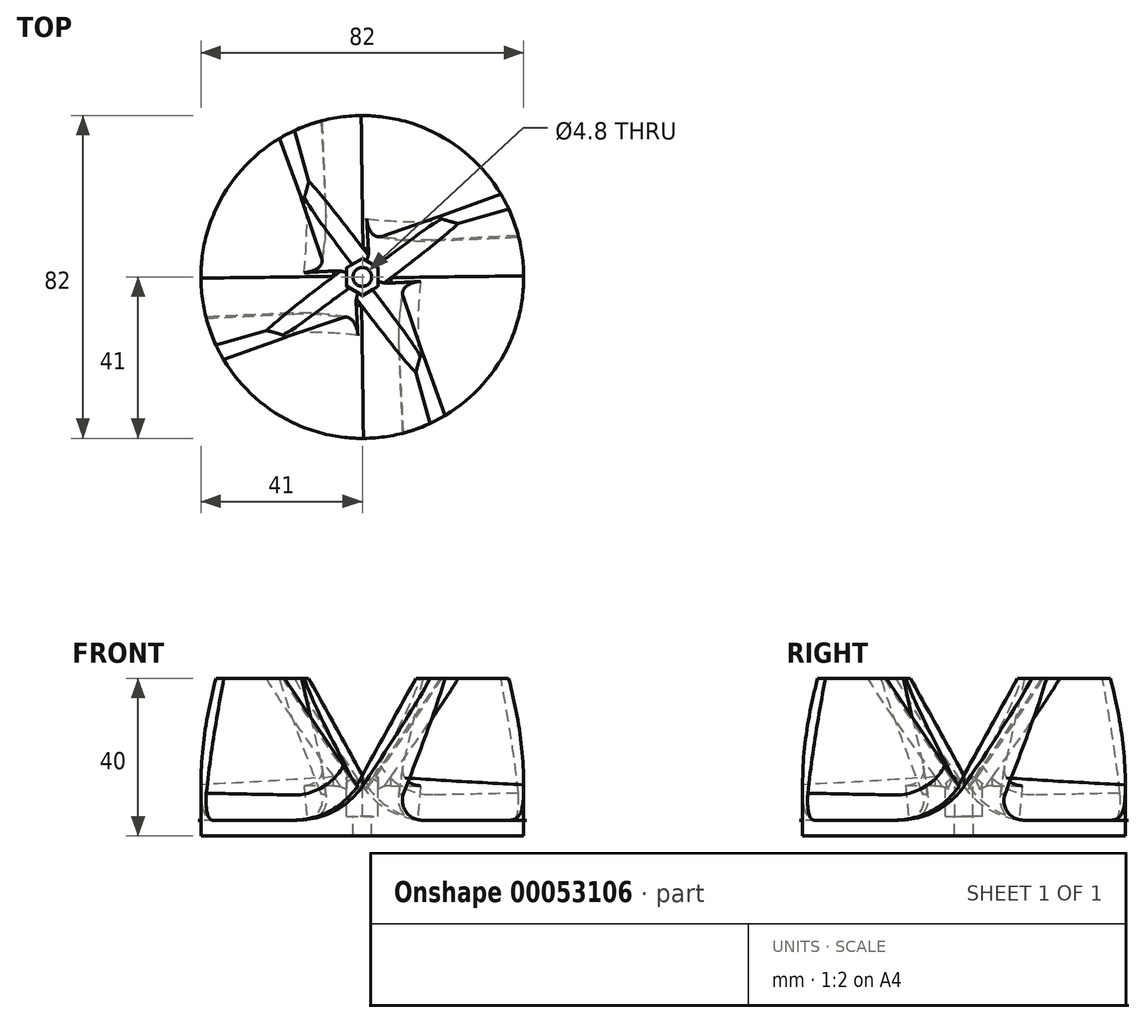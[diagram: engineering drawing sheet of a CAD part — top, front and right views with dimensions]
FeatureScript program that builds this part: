
annotation { "Feature Type Name" : "Feature", "Feature Type Description" : "" }
export const myFeature = defineFeature(function(context is Context, id is Id, definition is map)
    precondition{}
    {
        {
            var Q0;
            Q0=qCreatedBy(makeId("Top.planeOp"),FACE);
            var sketch = newSketch(context, id + "F0", { "sketchPlane" : qUnion([Q0])});
            skLineSegment(sketch, "E0.bottom", {"start": v(7.1, 8.27) * mm, "end": v(-43.93, 8.27) * mm});
            skLineSegment(sketch, "E0.top", {"start": v(7.1, -6.26) * mm, "end": v(-43.93, -6.26) * mm});
            skLineSegment(sketch, "E0.left", {"start": v(7.1, 8.27) * mm, "end": v(7.1, -6.26) * mm});
            skLineSegment(sketch, "E0.right", {"start": v(-43.93, 8.27) * mm, "end": v(-43.93, -6.26) * mm});
            skSolve(sketch);
        }
        {
            var Q0;
            Q0=qCreatedBy(makeId("Top.planeOp"),FACE);
            var sketch = newSketch(context, id + "F1", { "sketchPlane" : qUnion([Q0])});
            skCircle(sketch, "E1", {"center": v(0, 0) * mm, "radius": 41 * mm});
            skCircle(sketch, "E2", {"center": v(0, 0) * mm, "radius": 83.6 * mm});
            skSolve(sketch);
        }
        {
            var Q0;
            Q0=makeQuery(id+"F1.imprint","IMPRINT",FACE,{"disambiguationData":[TD([[makeQuery(id+"F1.imprint","IMPRINT",EDGE,{"derivedFrom":sQuery(id+"F1.wireOp",EDGE,"E1")}),1.0]])]});
            extrude(context, id + "F2", {"entities" : qUnion([Q0]), "depth" : 4 * mm});
        }
        {
            var Q0;
            Q0=qCreatedBy(makeId("Top.planeOp"),FACE);
            cPlane(context, id + "F3", {"entities" : qUnion([Q0]), "cplaneType" : CPlaneType.OFFSET, "offset" : 40 * mm, "width" : 150 * mm, "height" : 150 * mm});
        }
        {
            var Q0;
            Q0=qCreatedBy(id+"F3.planeOp",FACE);
            var sketch = newSketch(context, id + "F4", { "sketchPlane" : qUnion([Q0])});
            skCircle(sketch, "E3", {"center": v(0, 0) * mm, "radius": 25 * mm});
            skCircle(sketch, "E4", {"center": v(0, 0) * mm, "radius": 45 * mm});
            skLineSegment(sketch, "E5", {"start": v(-39.03, -22.4) * mm, "end": v(-19.7, -15.4) * mm});
            skLineSegment(sketch, "E6", {"start": v(-21.49, -12.78) * mm, "end": v(-41.08, -18.37) * mm});
            skCircle(sketch, "E7", {"center": v(0, 0) * mm, "radius": 2.4 * mm});
            skCircle(sketch, "E8.cCircle", {"center": v(0, 0) * mm, "radius": 4.05 * mm, "construction": true});
            skLineSegment(sketch, "E8.0", {"start": v(4.05, 2.34) * mm, "end": v(4.05, -2.34) * mm});
            skLineSegment(sketch, "E8.1", {"start": v(4.05, -2.34) * mm, "end": v(0, -4.68) * mm});
            skLineSegment(sketch, "E8.2", {"start": v(0, -4.68) * mm, "end": v(-4.05, -2.34) * mm});
            skLineSegment(sketch, "E8.3", {"start": v(-4.05, -2.34) * mm, "end": v(-4.05, 2.34) * mm});
            skLineSegment(sketch, "E8.4", {"start": v(-4.05, 2.34) * mm, "end": v(0, 4.68) * mm});
            skLineSegment(sketch, "E8.5", {"start": v(0, 4.68) * mm, "end": v(4.05, 2.34) * mm});
            skPoint(sketch, "E8.0.midPoint", {"position": v(4.05, 0) * mm});
            skSolve(sketch);
        }
        {
            var Q0;
            {var subQ1=sQuery(id+"F4.wireOp",EDGE,"E5");Q0=makeQuery(id+"F4.imprint","IMPRINT",FACE,{"disambiguationData":[TD([[makeQuery(id+"F4.imprint","IMPRINT",EDGE,{"derivedFrom":subQ1}),1.0]])]});}
            var Q1;
            {var subQ0=sQuery(id+"F0.wireOp",EDGE,"E0.left");Q1=makeQuery(id+"F0.imprint","IMPRINT",FACE,{"disambiguationData":[TD([[makeQuery(id+"F0.imprint","IMPRINT",EDGE,{"derivedFrom":subQ0}),-1.0]])]});}
            loft(context, id + "F5", {"sheetProfilesArray" : [{ "sheetProfileEntities" : qUnion([Q0]) }, { "sheetProfileEntities" : qUnion([Q1]) }]});
        }
        {
            var Q0;
            Q0=makeQuery(id+"F5.opLoft","SWEPT_EDGE",EDGE,{"disambiguationData":[OSD([sQuery(id+"F0.wireOp",EDGE,"E0.bottom"),sQuery(id+"F0.wireOp",EDGE,"E0.left"),sQuery(id+"F4.wireOp",EDGE,"E3"),sQuery(id+"F4.wireOp",EDGE,"E6")])]});
            chamfer(context, id + "F6", {"entities" : qUnion([Q0]), "width" : 3 * mm, "tangentPropagation" : true});
        }
        {
            var Q0;
            {var subQ1=sQuery(id+"F0.wireOp",EDGE,"2f4ce80c-512e-42e9-ad37-1b76bf56904e");var subQ4=sQuery(id+"F4.wireOp",EDGE,"E5");Q0=makeQuery(id+"F5.opLoft","SWEPT_BODY",BODY,{"disambiguationData":[OSD([makeQuery(id+"F0.imprint","IMPRINT",FACE,{"disambiguationData":[TD([[makeQuery(id+"F0.imprint","IMPRINT",EDGE,{"derivedFrom":subQ1}),-1.0]])]}),makeQuery(id+"F4.imprint","IMPRINT",FACE,{"disambiguationData":[TD([[makeQuery(id+"F4.imprint","IMPRINT",EDGE,{"derivedFrom":subQ4}),1.0]])]})])]});}
            var Q1;
            Q1=makeQuery(id+"F2.opExtrude","CAP_EDGE",EDGE,{"disambiguationData":[OSD([sQuery(id+"F1.wireOp",EDGE,"E1")])],"isStart":false});
            circularPattern(context, id + "F7", {"entities" : qUnion([Q0]), "axis" : qUnion([Q1]), "angle" : 90 * degree, "instanceCount" : round(4), "computeTransformsWithoutBuiltin" : true});
        }
        {
            var Q0;
            {var subQ4=sQuery(id+"F0.wireOp",EDGE,"5ef0fec1-321e-4ed4-9ece-5ae84b4b1e6a.bottom");var subQ6=sQuery(id+"F4.wireOp",EDGE,"E5");Q0=makeQuery(id+"F5.opLoft","SWEPT_BODY",BODY,{"disambiguationData":[OSD([makeQuery(id+"F0.imprint","IMPRINT",FACE,{"disambiguationData":[TD([[makeQuery(id+"F0.imprint","IMPRINT",EDGE,{"derivedFrom":subQ4}),-1.0]])]}),makeQuery(id+"F4.imprint","IMPRINT",FACE,{"disambiguationData":[TD([[makeQuery(id+"F4.imprint","IMPRINT",EDGE,{"derivedFrom":subQ6}),1.0]])]})])]});}
            var Q1;
            {var subQ4=sQuery(id+"F0.wireOp",EDGE,"5ef0fec1-321e-4ed4-9ece-5ae84b4b1e6a.bottom");var subQ6=sQuery(id+"F4.wireOp",EDGE,"E5");Q1=makeQuery(id+"F7.opPattern","COPY",BODY,{"derivedFrom":makeQuery(id+"F5.opLoft","SWEPT_BODY",BODY,{"disambiguationData":[OSD([makeQuery(id+"F0.imprint","IMPRINT",FACE,{"disambiguationData":[TD([[makeQuery(id+"F0.imprint","IMPRINT",EDGE,{"derivedFrom":subQ4}),-1.0]])]}),makeQuery(id+"F4.imprint","IMPRINT",FACE,{"disambiguationData":[TD([[makeQuery(id+"F4.imprint","IMPRINT",EDGE,{"derivedFrom":subQ6}),1.0]])]})])]}),"instanceName":"2"});}
            var Q2;
            {var subQ4=sQuery(id+"F0.wireOp",EDGE,"5ef0fec1-321e-4ed4-9ece-5ae84b4b1e6a.bottom");var subQ6=sQuery(id+"F4.wireOp",EDGE,"E5");Q2=makeQuery(id+"F7.opPattern","COPY",BODY,{"derivedFrom":makeQuery(id+"F5.opLoft","SWEPT_BODY",BODY,{"disambiguationData":[OSD([makeQuery(id+"F0.imprint","IMPRINT",FACE,{"disambiguationData":[TD([[makeQuery(id+"F0.imprint","IMPRINT",EDGE,{"derivedFrom":subQ4}),-1.0]])]}),makeQuery(id+"F4.imprint","IMPRINT",FACE,{"disambiguationData":[TD([[makeQuery(id+"F4.imprint","IMPRINT",EDGE,{"derivedFrom":subQ6}),1.0]])]})])]}),"instanceName":"1"});}
            var Q3;
            {var subQ4=sQuery(id+"F0.wireOp",EDGE,"5ef0fec1-321e-4ed4-9ece-5ae84b4b1e6a.bottom");var subQ6=sQuery(id+"F4.wireOp",EDGE,"E5");Q3=makeQuery(id+"F7.opPattern","COPY",BODY,{"derivedFrom":makeQuery(id+"F5.opLoft","SWEPT_BODY",BODY,{"disambiguationData":[OSD([makeQuery(id+"F0.imprint","IMPRINT",FACE,{"disambiguationData":[TD([[makeQuery(id+"F0.imprint","IMPRINT",EDGE,{"derivedFrom":subQ4}),-1.0]])]}),makeQuery(id+"F4.imprint","IMPRINT",FACE,{"disambiguationData":[TD([[makeQuery(id+"F4.imprint","IMPRINT",EDGE,{"derivedFrom":subQ6}),1.0]])]})])]}),"instanceName":"3"});}
            var Q4;
            Q4=makeQuery(id+"F2.opExtrude","SWEPT_BODY",BODY,{"disambiguationData":[OSD([sQuery(id+"F1.wireOp",EDGE,"E1")])]});
            booleanBodies(context, id + "F8", {"operationType" : BooleanOperationType.UNION, "tools" : qUnion([Q0, Q1, Q2, Q3, Q4])});
        }
        {
            var Q0;
            Q0=makeQuery(id+"F8.opBoolean","INTERSECT",EDGE,{"derivedFrom":[makeQuery(id+"F2.opExtrude","CAP_FACE",FACE,{"disambiguationData":[OSD([sQuery(id+"F1.wireOp",EDGE,"E1")])],"isStart":false}),makeQuery(id+"F5.opLoft","SWEPT_FACE",FACE,{"disambiguationData":[OSD([sQuery(id+"F0.wireOp",EDGE,"E0.bottom"),sQuery(id+"F0.wireOp",EDGE,"E0.left"),sQuery(id+"F0.wireOp",EDGE,"E0.right"),sQuery(id+"F4.wireOp",EDGE,"E3"),sQuery(id+"F4.wireOp",EDGE,"E4"),sQuery(id+"F4.wireOp",EDGE,"E6")])]})]});
            var Q1;
            Q1=makeQuery(id+"F8.opBoolean","INTERSECT",EDGE,{"derivedFrom":[makeQuery(id+"F2.opExtrude","CAP_FACE",FACE,{"disambiguationData":[OSD([sQuery(id+"F1.wireOp",EDGE,"E1")])],"isStart":false}),makeQuery(id+"F7.opPattern","COPY",FACE,{"derivedFrom":makeQuery(id+"F5.opLoft","SWEPT_FACE",FACE,{"disambiguationData":[OSD([sQuery(id+"F0.wireOp",EDGE,"E0.bottom"),sQuery(id+"F0.wireOp",EDGE,"E0.left"),sQuery(id+"F0.wireOp",EDGE,"E0.right"),sQuery(id+"F4.wireOp",EDGE,"E3"),sQuery(id+"F4.wireOp",EDGE,"E4"),sQuery(id+"F4.wireOp",EDGE,"E6")])]}),"instanceName":"3"})]});
            var Q2;
            Q2=makeQuery(id+"F8.opBoolean","INTERSECT",EDGE,{"derivedFrom":[makeQuery(id+"F2.opExtrude","CAP_FACE",FACE,{"disambiguationData":[OSD([sQuery(id+"F1.wireOp",EDGE,"E1")])],"isStart":false}),makeQuery(id+"F7.opPattern","COPY",FACE,{"derivedFrom":makeQuery(id+"F5.opLoft","SWEPT_FACE",FACE,{"disambiguationData":[OSD([sQuery(id+"F0.wireOp",EDGE,"E0.bottom"),sQuery(id+"F0.wireOp",EDGE,"E0.left"),sQuery(id+"F0.wireOp",EDGE,"E0.right"),sQuery(id+"F4.wireOp",EDGE,"E3"),sQuery(id+"F4.wireOp",EDGE,"E4"),sQuery(id+"F4.wireOp",EDGE,"E6")])]}),"instanceName":"1"})]});
            var Q3;
            Q3=makeQuery(id+"F8.opBoolean","INTERSECT",EDGE,{"derivedFrom":[makeQuery(id+"F2.opExtrude","CAP_FACE",FACE,{"disambiguationData":[OSD([sQuery(id+"F1.wireOp",EDGE,"E1")])],"isStart":false}),makeQuery(id+"F7.opPattern","COPY",FACE,{"derivedFrom":makeQuery(id+"F5.opLoft","SWEPT_FACE",FACE,{"disambiguationData":[OSD([sQuery(id+"F0.wireOp",EDGE,"E0.bottom"),sQuery(id+"F0.wireOp",EDGE,"E0.left"),sQuery(id+"F0.wireOp",EDGE,"E0.right"),sQuery(id+"F4.wireOp",EDGE,"E3"),sQuery(id+"F4.wireOp",EDGE,"E4"),sQuery(id+"F4.wireOp",EDGE,"E6")])]}),"instanceName":"2"})]});
            fillet(context, id + "F9", {"entities" : qUnion([Q0, Q1, Q2, Q3]), "radius" : 20 * mm, "tangentPropagation" : true, "allowEdgeOverflow" : false});
        }
        {
            var Q0;
            Q0=makeQuery(id+"F8.opBoolean","INTERSECT",EDGE,{"derivedFrom":[makeQuery(id+"F2.opExtrude","CAP_FACE",FACE,{"disambiguationData":[OSD([sQuery(id+"F1.wireOp",EDGE,"E1")])],"isStart":false}),makeQuery(id+"F5.opLoft","SWEPT_FACE",FACE,{"disambiguationData":[OSD([sQuery(id+"F0.wireOp",EDGE,"E0.top"),sQuery(id+"F0.wireOp",EDGE,"E0.left"),sQuery(id+"F0.wireOp",EDGE,"E0.right"),sQuery(id+"F4.wireOp",EDGE,"E3"),sQuery(id+"F4.wireOp",EDGE,"E4"),sQuery(id+"F4.wireOp",EDGE,"E5")])]})]});
            var Q1;
            Q1=makeQuery(id+"F8.opBoolean","INTERSECT",EDGE,{"derivedFrom":[makeQuery(id+"F2.opExtrude","CAP_FACE",FACE,{"disambiguationData":[OSD([sQuery(id+"F1.wireOp",EDGE,"E1")])],"isStart":false}),makeQuery(id+"F7.opPattern","COPY",FACE,{"derivedFrom":makeQuery(id+"F5.opLoft","SWEPT_FACE",FACE,{"disambiguationData":[OSD([sQuery(id+"F0.wireOp",EDGE,"E0.top"),sQuery(id+"F0.wireOp",EDGE,"E0.left"),sQuery(id+"F0.wireOp",EDGE,"E0.right"),sQuery(id+"F4.wireOp",EDGE,"E3"),sQuery(id+"F4.wireOp",EDGE,"E4"),sQuery(id+"F4.wireOp",EDGE,"E5")])]}),"instanceName":"1"})]});
            var Q2;
            Q2=makeQuery(id+"F8.opBoolean","INTERSECT",EDGE,{"derivedFrom":[makeQuery(id+"F2.opExtrude","CAP_FACE",FACE,{"disambiguationData":[OSD([sQuery(id+"F1.wireOp",EDGE,"E1")])],"isStart":false}),makeQuery(id+"F7.opPattern","COPY",FACE,{"derivedFrom":makeQuery(id+"F5.opLoft","SWEPT_FACE",FACE,{"disambiguationData":[OSD([sQuery(id+"F0.wireOp",EDGE,"E0.top"),sQuery(id+"F0.wireOp",EDGE,"E0.left"),sQuery(id+"F0.wireOp",EDGE,"E0.right"),sQuery(id+"F4.wireOp",EDGE,"E3"),sQuery(id+"F4.wireOp",EDGE,"E4"),sQuery(id+"F4.wireOp",EDGE,"E5")])]}),"instanceName":"2"})]});
            var Q3;
            Q3=makeQuery(id+"F8.opBoolean","INTERSECT",EDGE,{"derivedFrom":[makeQuery(id+"F2.opExtrude","CAP_FACE",FACE,{"disambiguationData":[OSD([sQuery(id+"F1.wireOp",EDGE,"E1")])],"isStart":false}),makeQuery(id+"F7.opPattern","COPY",FACE,{"derivedFrom":makeQuery(id+"F5.opLoft","SWEPT_FACE",FACE,{"disambiguationData":[OSD([sQuery(id+"F0.wireOp",EDGE,"E0.top"),sQuery(id+"F0.wireOp",EDGE,"E0.left"),sQuery(id+"F0.wireOp",EDGE,"E0.right"),sQuery(id+"F4.wireOp",EDGE,"E3"),sQuery(id+"F4.wireOp",EDGE,"E4"),sQuery(id+"F4.wireOp",EDGE,"E5")])]}),"instanceName":"3"})]});
            fillet(context, id + "F10", {"entities" : qUnion([Q0, Q1, Q2, Q3]), "radius" : 5 * mm, "tangentPropagation" : true, "allowEdgeOverflow" : false});
        }
        {
            var Q0;
            Q0=makeQuery(id+"F4.imprint","IMPRINT",FACE,{"disambiguationData":[TD([[makeQuery(id+"F4.imprint","IMPRINT",EDGE,{"derivedFrom":sQuery(id+"F4.wireOp",EDGE,"E7")}),1.0]])]});
            var Q1;
            {var subQ4=sQuery(id+"F0.wireOp",EDGE,"5ef0fec1-321e-4ed4-9ece-5ae84b4b1e6a.bottom");var subQ6=sQuery(id+"F4.wireOp",EDGE,"E5");Q1=makeQuery(id+"F7.opPattern","COPY",BODY,{"derivedFrom":makeQuery(id+"F5.opLoft","SWEPT_BODY",BODY,{"disambiguationData":[OSD([makeQuery(id+"F0.imprint","IMPRINT",FACE,{"disambiguationData":[TD([[makeQuery(id+"F0.imprint","IMPRINT",EDGE,{"derivedFrom":subQ4}),-1.0]])]}),makeQuery(id+"F4.imprint","IMPRINT",FACE,{"disambiguationData":[TD([[makeQuery(id+"F4.imprint","IMPRINT",EDGE,{"derivedFrom":subQ6}),1.0]])]})])]}),"instanceName":"2"});}
            extrude(context, id + "F11", {"entities" : qUnion([Q0]), "operationType" : NewBodyOperationType.REMOVE, "endBound" : BoundingType.THROUGH_ALL, "oppositeDirection" : true, "endBoundEntityBody" : qUnion([Q1]), "depth" : 25 * mm});
        }
        {
            var Q0;
            Q0=makeQuery(id+"F4.imprint","IMPRINT",FACE,{"disambiguationData":[TD([[makeQuery(id+"F4.imprint","IMPRINT",EDGE,{"derivedFrom":sQuery(id+"F4.wireOp",EDGE,"E7")}),-1.0]])]});
            extrude(context, id + "F12", {"entities" : qUnion([Q0]), "operationType" : NewBodyOperationType.REMOVE, "oppositeDirection" : true, "depth" : 35 * mm});
        }
        {
            var Q0;
            Q0=makeQuery(id+"F1.imprint","IMPRINT",FACE,{"disambiguationData":[TD([[makeQuery(id+"F1.imprint","IMPRINT",EDGE,{"derivedFrom":sQuery(id+"F1.wireOp",EDGE,"E1")}),-1.0]])]});
            extrude(context, id + "F13", {"entities" : qUnion([Q0]), "operationType" : NewBodyOperationType.REMOVE, "depth" : 50 * mm});
        }
    });
